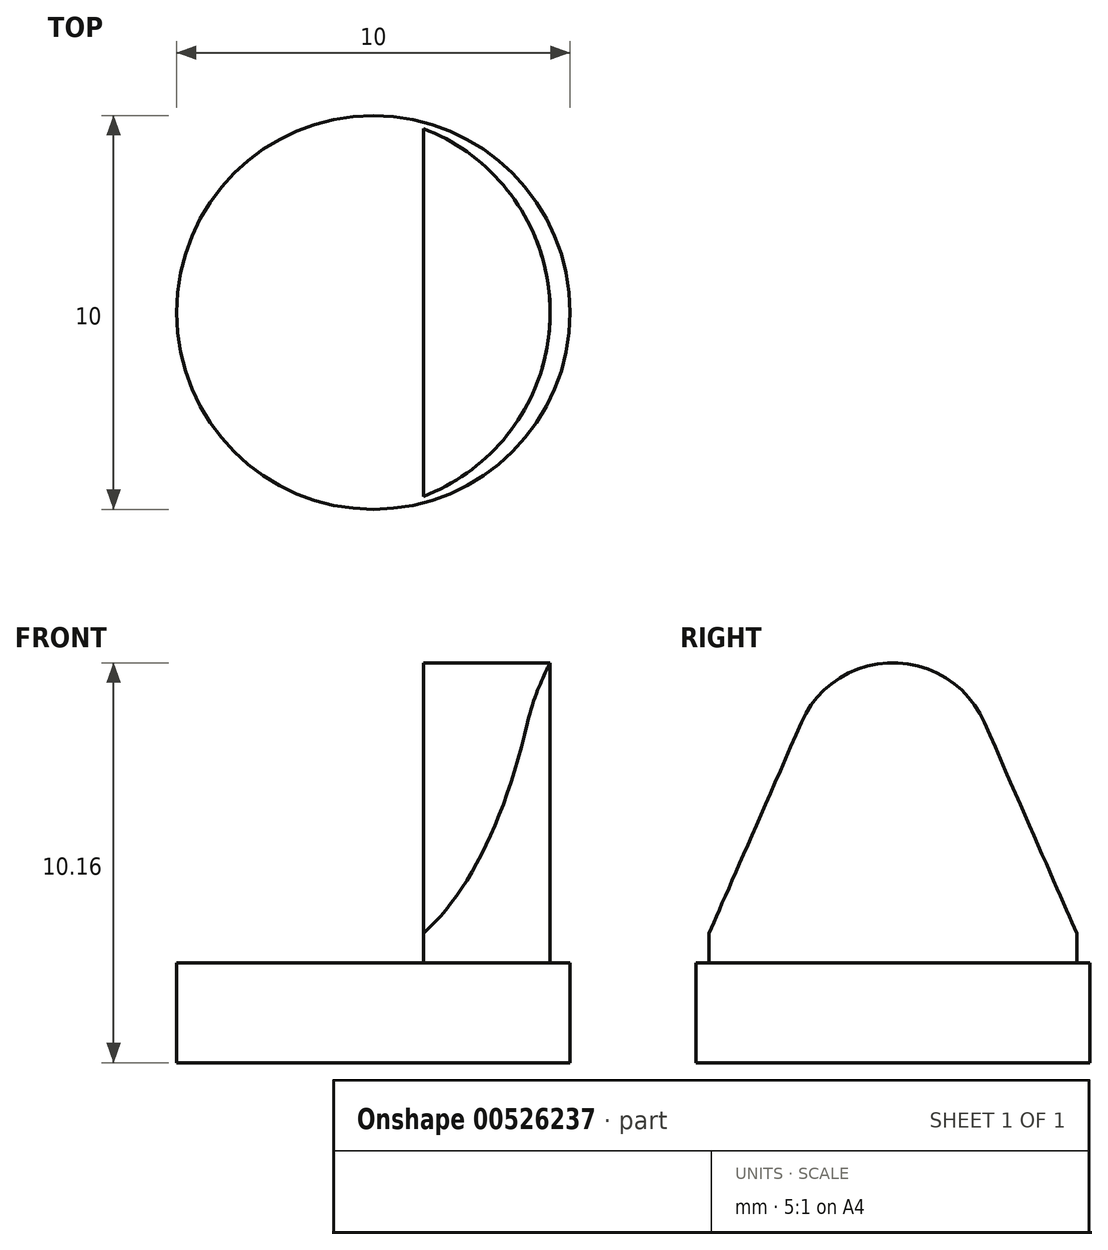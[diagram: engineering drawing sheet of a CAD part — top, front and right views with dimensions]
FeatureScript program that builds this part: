
annotation { "Feature Type Name" : "Feature", "Feature Type Description" : "" }
export const myFeature = defineFeature(function(context is Context, id is Id, definition is map)
    precondition{}
    {
        {
            var Q0;
            Q0=qCreatedBy(makeId("Top.planeOp"),FACE);
            var sketch = newSketch(context, id + "F0", { "sketchPlane" : qUnion([Q0])});
            skCircle(sketch, "E0", {"center": v(0, 0) * mm, "radius": 5 * mm});
            skSolve(sketch);
        }
        {
            var Q0;
            Q0=makeQuery(id+"F0.imprint","IMPRINT",FACE,{"disambiguationData":[TD([[makeQuery(id+"F0.imprint","IMPRINT",EDGE,{"derivedFrom":sQuery(id+"F0.wireOp",EDGE,"E0")}),1.0]])]});
            var Q1;
            Q1=sQuery(id+"F0.wireOp",EDGE,"E0");
            extrude(context, id + "F1", {"entities" : qUnion([Q0]), "surfaceEntities" : qUnion([Q1]), "depth" : 2.54 * mm, "offsetDistance" : 25.4 * mm});
        }
        {
            var Q0;
            Q0=qCreatedBy(makeId("Right.planeOp"),FACE);
            var sketch = newSketch(context, id + "F2", { "sketchPlane" : qUnion([Q0])});
            skArc(sketch, "E1", {"start": v(2.33, 8.64) * mm, "mid": v(0, 10.16) * mm, "end": v(-2.33, 8.64) * mm});
            skLineSegment(sketch, "E2", {"start": v(-2.33, 8.64) * mm, "end": v(-5, 2.54) * mm});
            skLineSegment(sketch, "E3.MirrorCS", {"start": v(2.33, 8.64) * mm, "end": v(5, 2.54) * mm});
            skLineSegment(sketch, "E4", {"start": v(5, 2.54) * mm, "end": v(-5, 2.54) * mm});
            skSolve(sketch);
        }
        {
            var Q0;
            Q0 = qSketchRegion(id + "F2", true);
            var Q1;
            Q1=makeQuery(id+"F1.opExtrude","SWEPT_FACE",FACE,{"disambiguationData":[OSD([sQuery(id+"F0.wireOp",EDGE,"E0")])]});
            extrude(context, id + "F3", {"entities" : qUnion([Q0]), "operationType" : NewBodyOperationType.ADD, "endBound" : BoundingType.UP_TO_SURFACE, "depth" : 25.4 * mm, "endBoundEntityFace" : qUnion([Q1]), "hasOffset" : true, "offsetDistance" : 0.5 * mm, "hasSecondDirection" : true, "secondDirectionOppositeDirection" : false, "secondDirectionDepth" : 1.27 * mm});
        }
        {
            var Q0;
            Q0=sQuery(id+"F2.wireOp",VERTEX,"E1.center");
            var Q1;
            Q1=makeQuery(id+"F1.opExtrude","SWEPT_BODY",BODY,{"disambiguationData":[OSD([sQuery(id+"F0.wireOp",EDGE,"E0")])]});
            hole(context, id + "F4", {"style" : HoleStyle.C_BORE, "endStyle" : HoleEndStyle.THROUGH, "holeDiameter" : 2.54 * mm, "cBoreDiameter" : 3.05 * mm, "cBoreDepth" : 1.52 * mm, "isTappedThrough" : true, "tappedDepth" : 12.7 * mm, "tapClearance" : 3, "startFromSketch" : true, "locations" : qUnion([Q0]), "scope" : qUnion([Q1])});
        }
    });
